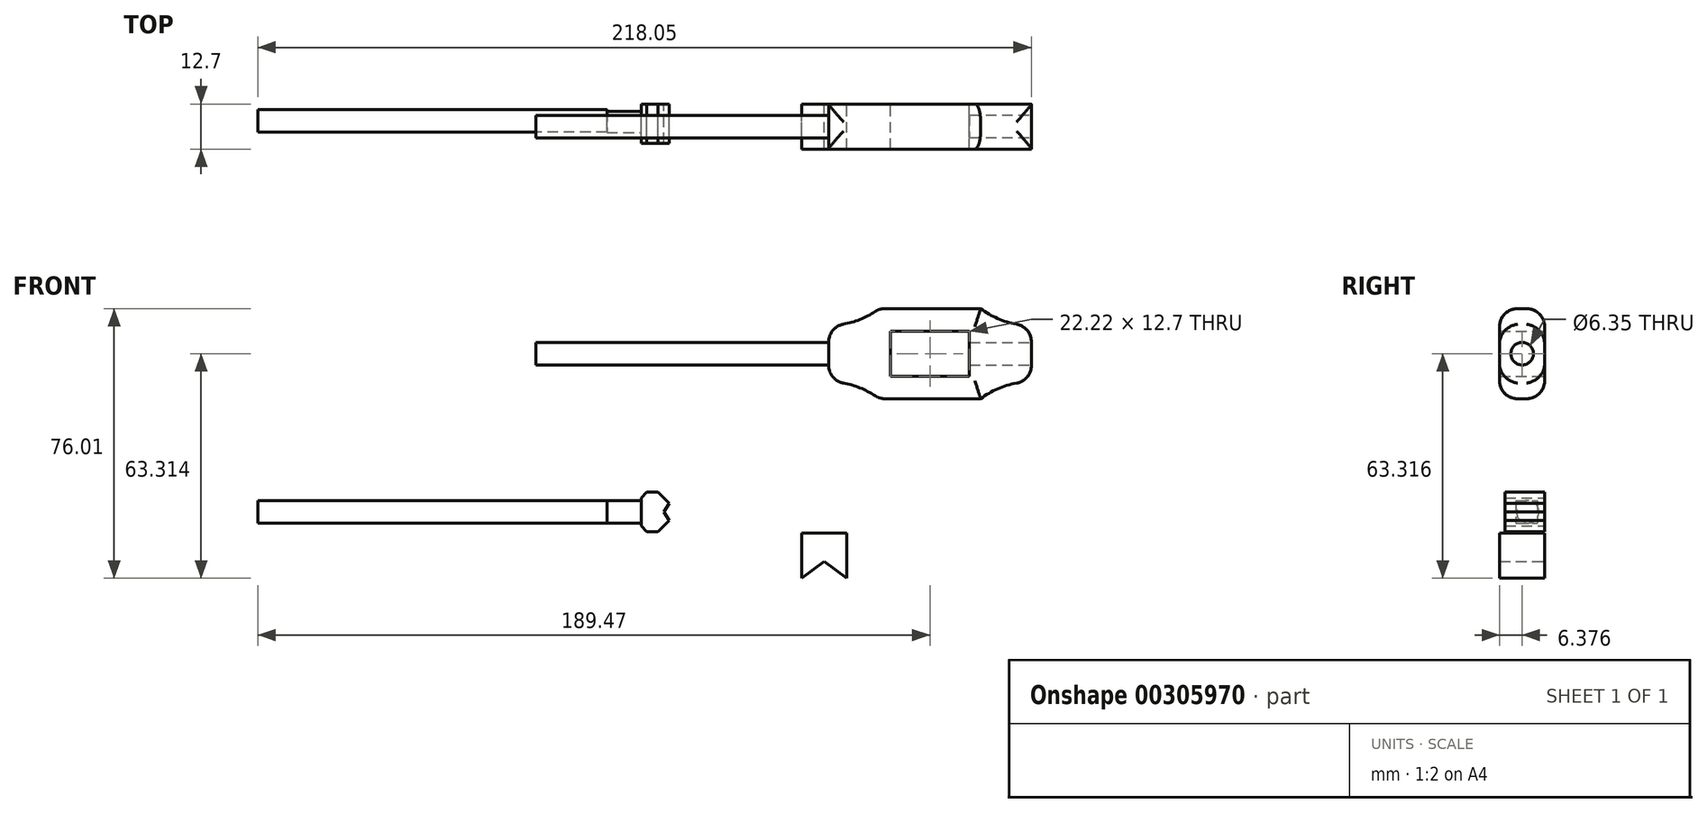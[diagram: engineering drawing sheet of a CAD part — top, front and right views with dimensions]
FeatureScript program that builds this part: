
annotation { "Feature Type Name" : "Feature", "Feature Type Description" : "" }
export const myFeature = defineFeature(function(context is Context, id is Id, definition is map)
    precondition{}
    {
        {
            var Q0;
            Q0=qCreatedBy(makeId("Front.planeOp"),FACE);
            var sketch = newSketch(context, id + "F0", { "sketchPlane" : qUnion([Q0])});
            skLineSegment(sketch, "E0", {"start": v(-67.47, 40.3) * mm, "end": v(-67.47, 24.42) * mm});
            skLineSegment(sketch, "E1", {"start": v(-53.19, 19.65) * mm, "end": v(-24.61, 19.65) * mm});
            skPoint(sketch, "E2.endSnap0", {"position": v(-38.9, 19.65) * mm});
            skLineSegment(sketch, "E3", {"start": v(-10.32, 24.42) * mm, "end": v(-10.32, 40.3) * mm});
            skLineSegment(sketch, "E4", {"start": v(-24.61, 45.05) * mm, "end": v(-53.19, 45.05) * mm});
            skArc(sketch, "E5", {"start": v(-67.47, 40.3) * mm, "mid": v(-59.94, 41.51) * mm, "end": v(-53.19, 45.05) * mm});
            skArc(sketch, "E6", {"start": v(-53.19, 19.65) * mm, "mid": v(-59.94, 23.2) * mm, "end": v(-67.47, 24.42) * mm});
            skArc(sketch, "E7", {"start": v(-24.61, 45.05) * mm, "mid": v(-17.85, 41.51) * mm, "end": v(-10.32, 40.3) * mm});
            skArc(sketch, "E8", {"start": v(-10.32, 24.42) * mm, "mid": v(-17.85, 23.2) * mm, "end": v(-24.61, 19.65) * mm});
            skLineSegment(sketch, "E9", {"start": v(-50.01, 38.7) * mm, "end": v(-27.79, 38.7) * mm});
            skLineSegment(sketch, "E10", {"start": v(-27.79, 38.7) * mm, "end": v(-27.79, 26) * mm});
            skLineSegment(sketch, "E11", {"start": v(-27.79, 26) * mm, "end": v(-50.01, 26) * mm});
            skLineSegment(sketch, "E12", {"start": v(-50.01, 26) * mm, "end": v(-50.01, 38.7) * mm});
            skLineSegment(sketch, "E13", {"start": v(-67.47, 40.3) * mm, "end": v(-67.47, 38.7) * mm});
            skLineSegment(sketch, "E14", {"start": v(-67.47, 24.42) * mm, "end": v(-67.47, 26) * mm});
            skLineSegment(sketch, "E15", {"start": v(-67.47, 26) * mm, "end": v(-150.02, 26) * mm});
            skLineSegment(sketch, "E16", {"start": v(-150.02, 26) * mm, "end": v(-150.02, 38.7) * mm});
            skLineSegment(sketch, "E17", {"start": v(-150.02, 38.7) * mm, "end": v(-67.47, 38.7) * mm});
            skLineSegment(sketch, "E18", {"start": v(-129.94, -9.07) * mm, "end": v(-129.94, -15.42) * mm});
            skLineSegment(sketch, "E19", {"start": v(-129.94, -15.42) * mm, "end": v(-120.3, -15.42) * mm});
            skLineSegment(sketch, "E20", {"start": v(-120.3, -15.42) * mm, "end": v(-120.3, -9.07) * mm});
            skLineSegment(sketch, "E21", {"start": v(-120.3, -9.07) * mm, "end": v(-129.94, -9.07) * mm});
            skLineSegment(sketch, "E22", {"start": v(-129.94, -9.07) * mm, "end": v(-129.94, -7.48) * mm});
            skLineSegment(sketch, "E23", {"start": v(-129.94, -7.48) * mm, "end": v(-152.17, -7.48) * mm});
            skLineSegment(sketch, "E24", {"start": v(-129.94, -15.42) * mm, "end": v(-129.94, -17) * mm});
            skLineSegment(sketch, "E25", {"start": v(-129.94, -17) * mm, "end": v(-152.17, -17) * mm});
            skLineSegment(sketch, "E26", {"start": v(-152.17, -17) * mm, "end": v(-152.17, -7.48) * mm});
            skLineSegment(sketch, "E27", {"start": v(-152.17, -7.48) * mm, "end": v(-152.17, -5.9) * mm});
            skLineSegment(sketch, "E28", {"start": v(-152.17, -17) * mm, "end": v(-152.17, -18.6) * mm});
            skLineSegment(sketch, "E29", {"start": v(-152.17, -18.6) * mm, "end": v(-228.37, -18.6) * mm});
            skLineSegment(sketch, "E30", {"start": v(-228.37, -18.6) * mm, "end": v(-228.37, -5.9) * mm});
            skLineSegment(sketch, "E31", {"start": v(-228.37, -5.9) * mm, "end": v(-152.17, -5.9) * mm});
            skLineSegment(sketch, "E32", {"start": v(-120.3, -9.07) * mm, "end": v(-120.3, -8.27) * mm});
            skLineSegment(sketch, "E33", {"start": v(-120.3, -15.42) * mm, "end": v(-120.3, -16.21) * mm});
            skLineSegment(sketch, "E34", {"start": v(-118.7, -17.8) * mm, "end": v(-120.3, -16.21) * mm});
            skLineSegment(sketch, "E35", {"start": v(-118.7, -6.69) * mm, "end": v(-120.3, -8.27) * mm});
            skLineSegment(sketch, "E36", {"start": v(-118.7, -17.8) * mm, "end": v(-115.53, -17.8) * mm});
            skLineSegment(sketch, "E37", {"start": v(-118.7, -6.69) * mm, "end": v(-115.53, -6.69) * mm});
            skLineSegment(sketch, "E38", {"start": v(-112.36, -9.86) * mm, "end": v(-115.53, -6.69) * mm});
            skLineSegment(sketch, "E39", {"start": v(-112.36, -14.62) * mm, "end": v(-115.53, -17.8) * mm});
            skPoint(sketch, "E40.endSnap0", {"position": v(-113.95, -8.27) * mm});
            skLineSegment(sketch, "E41", {"start": v(-112.36, -9.86) * mm, "end": v(-113.95, -12.24) * mm});
            skLineSegment(sketch, "E42", {"start": v(-112.36, -14.62) * mm, "end": v(-113.95, -12.24) * mm});
            skSolve(sketch);
        }
        {
            var Q0;
            Q0=qCreatedBy(makeId("Front.planeOp"),FACE);
            var sketch = newSketch(context, id + "F1", { "sketchPlane" : qUnion([Q0])});
            skLineSegment(sketch, "E43", {"start": v(-62.35, -30.96) * mm, "end": v(-62.35, -18.26) * mm});
            skLineSegment(sketch, "E44", {"start": v(-62.35, -18.26) * mm, "end": v(-75.05, -18.26) * mm});
            skLineSegment(sketch, "E45", {"start": v(-75.05, -18.26) * mm, "end": v(-75.05, -30.96) * mm});
            skLineSegment(sketch, "E46", {"start": v(-62.35, -30.96) * mm, "end": v(-68.7, -26.2) * mm});
            skLineSegment(sketch, "E47", {"start": v(-75.05, -30.96) * mm, "end": v(-68.7, -26.2) * mm});
            skSolve(sketch);
        }
        {
            var Q0;
            Q0=makeQuery(id+"F1.imprint","IMPRINT",FACE,{"disambiguationData":[TD([[makeQuery(id+"F1.imprint","IMPRINT",EDGE,{"derivedFrom":sQuery(id+"F1.wireOp",EDGE,"E43")}),1.0]])]});
            extrude(context, id + "F2", {"entities" : qUnion([Q0]), "depth" : 12.7 * mm});
        }
        {
            var Q0;
            Q0=makeQuery(id+"F0.imprint","IMPRINT",FACE,{"disambiguationData":[TD([[makeQuery(id+"F0.imprint","IMPRINT",EDGE,{"derivedFrom":sQuery(id+"F0.wireOp",EDGE,"E0")}),1.0]])]});
            extrude(context, id + "F3", {"entities" : qUnion([Q0]), "depth" : 12.7 * mm});
        }
        {
            var Q0;
            Q0=makeQuery(id+"F0.imprint","IMPRINT",FACE,{"disambiguationData":[TD([[makeQuery(id+"F0.imprint","IMPRINT",EDGE,{"derivedFrom":sQuery(id+"F0.wireOp",EDGE,"E26")}),1.0]])]});
            extrude(context, id + "F4", {"entities" : qUnion([Q0]), "depth" : 9.52 * mm});
        }
        {
            var Q0;
            Q0=makeQuery(id+"F0.imprint","IMPRINT",FACE,{"disambiguationData":[TD([[makeQuery(id+"F0.imprint","IMPRINT",EDGE,{"derivedFrom":sQuery(id+"F0.wireOp",EDGE,"E18")}),1.0]])]});
            extrude(context, id + "F5", {"entities" : qUnion([Q0]), "operationType" : NewBodyOperationType.ADD, "depth" : 8.1 * mm, "hasSecondDirection" : true, "secondDirectionOppositeDirection" : true, "secondDirectionDepth" : -2.06 * mm});
        }
        {
            var Q0;
            Q0=makeQuery(id+"F0.imprint","IMPRINT",FACE,{"disambiguationData":[TD([[makeQuery(id+"F0.imprint","IMPRINT",EDGE,{"derivedFrom":sQuery(id+"F0.wireOp",EDGE,"E20")}),-1.0]])]});
            extrude(context, id + "F6", {"entities" : qUnion([Q0]), "operationType" : NewBodyOperationType.ADD, "depth" : 11.1 * mm});
        }
        {
            var Q0;
            Q0=makeQuery(id+"F3.opExtrude","SWEPT_FACE",FACE,{"disambiguationData":[OSD([sQuery(id+"F0.wireOp",EDGE,"E0"),sQuery(id+"F0.wireOp",EDGE,"E13"),sQuery(id+"F0.wireOp",EDGE,"E14")])]});
            var sketch = newSketch(context, id + "F7", { "sketchPlane" : qUnion([Q0])});
            skLineSegment(sketch, "E48", {"start": v(0, 24.42) * mm, "end": v(0, 32.35) * mm});
            skLineSegment(sketch, "E49", {"start": v(0, 40.3) * mm, "end": v(6.35, 40.3) * mm});
            skLineSegment(sketch, "E50", {"start": v(6.35, 40.3) * mm, "end": v(6.35, 32.35) * mm});
            skCircle(sketch, "E51", {"center": v(6.35, 32.35) * mm, "radius": 3.18 * mm});
            skSolve(sketch);
        }
        {
            var Q0;
            Q0=makeQuery(id+"F7.imprint","IMPRINT",FACE,{"disambiguationData":[TD([[makeQuery(id+"F7.imprint","IMPRINT",EDGE,{"derivedFrom":sQuery(id+"F7.wireOp",EDGE,"E51")}),1.0]])]});
            extrude(context, id + "F8", {"entities" : qUnion([Q0]), "operationType" : NewBodyOperationType.ADD, "depth" : 82.55 * mm});
        }
        {
            var Q0;
            Q0=makeQuery(id+"F4.opExtrude","SWEPT_FACE",FACE,{"disambiguationData":[OSD([sQuery(id+"F0.wireOp",EDGE,"E26"),sQuery(id+"F0.wireOp",EDGE,"E27"),sQuery(id+"F0.wireOp",EDGE,"E28")])]});
            var sketch = newSketch(context, id + "F9", { "sketchPlane" : qUnion([Q0])});
            skLineSegment(sketch, "E52", {"start": v(-9.53, -5.9) * mm, "end": v(-4.76, -5.9) * mm});
            skLineSegment(sketch, "E53", {"start": v(-9.53, -5.9) * mm, "end": v(-9.53, -12.24) * mm});
            skLineSegment(sketch, "E54", {"start": v(-9.53, -12.24) * mm, "end": v(-4.76, -12.24) * mm});
            skCircle(sketch, "E55", {"center": v(-4.76, -12.24) * mm, "radius": 3.18 * mm});
            skSolve(sketch);
        }
        {
            var Q0;
            Q0=makeQuery(id+"F9.imprint","IMPRINT",FACE,{"disambiguationData":[TD([[makeQuery(id+"F9.imprint","IMPRINT",EDGE,{"derivedFrom":sQuery(id+"F9.wireOp",EDGE,"E55")}),1.0]])]});
            extrude(context, id + "F10", {"entities" : qUnion([Q0]), "depth" : 22.22 * mm});
        }
        {
            var Q0;
            Q0=makeQuery(id+"F3.opExtrude","CAP_EDGE",EDGE,{"disambiguationData":[OSD([sQuery(id+"F0.wireOp",EDGE,"E5")])],"isStart":false});
            var Q1;
            Q1=makeQuery(id+"F3.opExtrude","CAP_EDGE",EDGE,{"disambiguationData":[OSD([sQuery(id+"F0.wireOp",EDGE,"E5")])],"isStart":true});
            var Q2;
            Q2=makeQuery(id+"F3.opExtrude","CAP_EDGE",EDGE,{"disambiguationData":[OSD([sQuery(id+"F0.wireOp",EDGE,"E4")])],"isStart":false});
            var Q3;
            Q3=makeQuery(id+"F3.opExtrude","CAP_EDGE",EDGE,{"disambiguationData":[OSD([sQuery(id+"F0.wireOp",EDGE,"E4")])],"isStart":true});
            var Q4;
            Q4=makeQuery(id+"F3.opExtrude","CAP_EDGE",EDGE,{"disambiguationData":[OSD([sQuery(id+"F0.wireOp",EDGE,"E7")])],"isStart":true});
            var Q5;
            Q5=makeQuery(id+"F3.opExtrude","CAP_EDGE",EDGE,{"disambiguationData":[OSD([sQuery(id+"F0.wireOp",EDGE,"E7")])],"isStart":false});
            var Q6;
            Q6=makeQuery(id+"F3.opExtrude","CAP_EDGE",EDGE,{"disambiguationData":[OSD([sQuery(id+"F0.wireOp",EDGE,"E8")])],"isStart":false});
            var Q7;
            Q7=makeQuery(id+"F3.opExtrude","CAP_EDGE",EDGE,{"disambiguationData":[OSD([sQuery(id+"F0.wireOp",EDGE,"E8")])],"isStart":true});
            var Q8;
            Q8=makeQuery(id+"F3.opExtrude","CAP_EDGE",EDGE,{"disambiguationData":[OSD([sQuery(id+"F0.wireOp",EDGE,"E1")])],"isStart":true});
            var Q9;
            Q9=makeQuery(id+"F3.opExtrude","CAP_EDGE",EDGE,{"disambiguationData":[OSD([sQuery(id+"F0.wireOp",EDGE,"E1")])],"isStart":false});
            var Q10;
            Q10=makeQuery(id+"F3.opExtrude","CAP_EDGE",EDGE,{"disambiguationData":[OSD([sQuery(id+"F0.wireOp",EDGE,"E6")])],"isStart":false});
            var Q11;
            Q11=makeQuery(id+"F3.opExtrude","CAP_EDGE",EDGE,{"disambiguationData":[OSD([sQuery(id+"F0.wireOp",EDGE,"E6")])],"isStart":true});
            var Q12;
            Q12=makeQuery(id+"F3.opExtrude","SWEPT_EDGE",EDGE,{"disambiguationData":[OSD([sQuery(id+"F0.wireOp",EDGE,"E5"),sQuery(id+"F0.wireOp",EDGE,"E13")])]});
            var Q13;
            Q13=makeQuery(id+"F3.opExtrude","SWEPT_EDGE",EDGE,{"disambiguationData":[OSD([sQuery(id+"F0.wireOp",EDGE,"E6"),sQuery(id+"F0.wireOp",EDGE,"E14")])]});
            var Q14;
            Q14=makeQuery(id+"F3.opExtrude","SWEPT_EDGE",EDGE,{"disambiguationData":[OSD([sQuery(id+"F0.wireOp",EDGE,"E3"),sQuery(id+"F0.wireOp",EDGE,"E7")])]});
            var Q15;
            Q15=makeQuery(id+"F3.opExtrude","SWEPT_EDGE",EDGE,{"disambiguationData":[OSD([sQuery(id+"F0.wireOp",EDGE,"E3"),sQuery(id+"F0.wireOp",EDGE,"E8")])]});
            fillet(context, id + "F11", {"entities" : qUnion([Q0, Q1, Q2, Q3, Q4, Q5, Q6, Q7, Q8, Q9, Q10, Q11, Q12, Q13, Q14, Q15]), "radius" : 5.08 * mm, "tangentPropagation" : true, "allowEdgeOverflow" : false});
        }
        {
            var Q0;
            Q0=makeQuery(id+"F4.opExtrude","SWEPT_BODY",BODY,{"disambiguationData":[OSD([sQuery(id+"F0.wireOp",EDGE,"E26"),sQuery(id+"F0.wireOp",EDGE,"E27"),sQuery(id+"F0.wireOp",EDGE,"E28"),sQuery(id+"F0.wireOp",EDGE,"E29"),sQuery(id+"F0.wireOp",EDGE,"E30"),sQuery(id+"F0.wireOp",EDGE,"E31")])]});
            deleteBodies(context, id + "F12", {"entities" : qUnion([Q0])});
        }
        {
            var Q0;
            Q0=makeQuery(id+"F10.opExtrude","CAP_FACE",FACE,{"disambiguationData":[OSD([sQuery(id+"F9.wireOp",EDGE,"E55")])],"isStart":true});
            var sketch = newSketch(context, id + "F13", { "sketchPlane" : qUnion([Q0])});
            skCircle(sketch, "E56", {"center": v(4.76, -12.24) * mm, "radius": 3.18 * mm});
            skSolve(sketch);
        }
        {
            var Q0;
            Q0=makeQuery(id+"F13.imprint","IMPRINT",FACE,{"disambiguationData":[TD([[makeQuery(id+"F13.imprint","IMPRINT",EDGE,{"derivedFrom":sQuery(id+"F13.wireOp",EDGE,"E56")}),-1.0]])]});
            extrude(context, id + "F14", {"entities" : qUnion([Q0]), "operationType" : NewBodyOperationType.ADD, "depth" : 76.2 * mm});
        }
        {
            var Q0;
            Q0=makeQuery(id+"F3.opExtrude","SWEPT_FACE",FACE,{"disambiguationData":[OSD([sQuery(id+"F0.wireOp",EDGE,"E3")])]});
            var sketch = newSketch(context, id + "F15", { "sketchPlane" : qUnion([Q0])});
            skLineSegment(sketch, "E57", {"start": v(-12.68, 29.05) * mm, "end": v(-12.68, 32.35) * mm});
            skPoint(sketch, "E57.endSnap0", {"position": v(-12.7, 32.35) * mm});
            skLineSegment(sketch, "E58", {"start": v(-12.68, 32.35) * mm, "end": v(-6.33, 32.35) * mm});
            skPoint(sketch, "E58.endSnap0", {"position": v(0, 32.35) * mm});
            skSolve(sketch);
        }
        {
            var Q0;
            {var subQ0=sQuery(id+"F0.wireOp",EDGE,"E3");Q0=makeQuery(id+"F15.imprint","IMPRINT",FACE,{"disambiguationData":[TD([[makeQuery(id+"F15.imprint","IMPRINT",EDGE,{"derivedFrom":makeQuery(id+"F3.opExtrude","CAP_EDGE",EDGE,{"disambiguationData":[OSD([subQ0])],"isStart":true})}),1.0]])]});}
            var sketch = newSketch(context, id + "F16", { "sketchPlane" : qUnion([Q0])});
            skCircle(sketch, "E59", {"center": v(-6.32, 32.36) * mm, "radius": 3.18 * mm});
            skSolve(sketch);
        }
        {
            var Q0;
            Q0=makeQuery(id+"F16.imprint","IMPRINT",FACE,{"disambiguationData":[TD([[makeQuery(id+"F16.imprint","IMPRINT",EDGE,{"derivedFrom":sQuery(id+"F16.wireOp",EDGE,"E59")}),1.0]])]});
            extrude(context, id + "F17", {"entities" : qUnion([Q0]), "operationType" : NewBodyOperationType.REMOVE, "oppositeDirection" : true, "depth" : 25.4 * mm});
        }
    });
